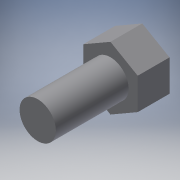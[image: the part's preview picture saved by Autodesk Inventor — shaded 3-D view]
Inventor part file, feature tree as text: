
AUTODESK INVENTOR PART (.ipt)
format: ipt  version: 2016 (Build 200138000, 138)  size: 99,328 bytes
history: native  units: in
note: dims shown in document units (in); Inventor stores cm internally (conversion verified against a paired STEP export)
features: extrude x2, sketch x2
ambient origin geometry x8: Origin, YZ Plane, XZ Plane, XY Plane, X Axis, Y Axis, Z Axis, Center Point
bodies: Solid1 (feature_tree)
feature tree (4):
  extrude  "Extrusion1"  Depth=0.4375in TaperAngle=0.0deg
  extrude  "Extrusion2"  Depth=1.0in TaperAngle=0.0deg
  sketch  "Sketch1"  dims[d0=0.75in d1=0.4375in d2=0.0in]
  sketch  "Sketch2"  dims[d3=0.5in d4=1.0in d5=0.0in]
